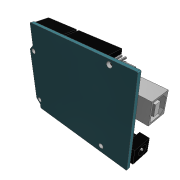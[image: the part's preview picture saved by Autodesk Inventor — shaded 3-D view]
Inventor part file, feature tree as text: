
AUTODESK INVENTOR PART (.ipt)
format: ipt  version: 2014 (Build 180170000, 170)  size: 910,848 bytes
history: native  units: mm
features: sketch x32, extrude x31, hole x1, chamfer x1, pattern_linear x1, plane x1, mirror x1, fillet x1
ambient origin geometry x8: Origin, YZ Plane, XZ Plane, XY Plane, X Axis, Y Axis, Z Axis, Center Point
bodies: Solid1 (feature_tree)
feature tree (69):
  extrude  "Extrusion1"  Depth=3.0mm
  extrude  "Extrusion2"  Depth=3.0mm
  extrude  "Extrusion3"  Depth=65.5mm
  extrude  "Extrusion4"  Depth=38.0mm
  extrude  "Extrusion5"  Depth=0.5mm
  extrude  "Extrusion6"  Depth=6.2mm
  extrude  "Extrusion7"  Depth=2.0mm TaperAngle=0.0deg
  hole  "Hole1"  [1 undecoded]
  extrude  "Extrusion8"  Depth=0.8mm
  extrude  "Extrusion9"  Depth=0.8mm
  extrude  "Extrusion10"  Depth=2.0mm
  extrude  "Extrusion11"  Depth=0.02mm TaperAngle=90.0deg
  extrude  "Extrusion12"  Depth=16.3mm
  extrude  "Extrusion13"  Depth=11.0mm TaperAngle=0.0deg
  extrude  "Extrusion14"  Depth=1.0mm
  extrude  "Extrusion15"  Depth=7.0mm
  extrude  "Extrusion16"  Depth=9.0mm TaperAngle=0.0deg
  extrude  "Extrusion17"  Depth=3.2mm
  extrude  "Extrusion18"  Depth=3.0mm
  extrude  "Extrusion19"  Depth=3.0mm
  chamfer  "Chamfer1"  Distance=11.0mm
  extrude  "Extrusion20"  Depth=8.0mm TaperAngle=0.0deg
  pattern_linear  "Rectangular Pattern1"  Spacing1=2.5mm  [1 undecoded]
  plane  "Work Plane1"
  mirror  "Mirror1"
  extrude  "Extrusion21"  Depth=13.5mm
  extrude  "Extrusion22"  Depth=0.75mm
  extrude  "Extrusion23"  Depth=1.0mm
  extrude  "Extrusion24"  Depth=2.65mm
  extrude  "Extrusion25"  Depth=1.0mm TaperAngle=0.0deg
  extrude  "Extrusion26"  Depth=0.75mm
  extrude  "Extrusion27"  Depth=1.0mm
  extrude  "Extrusion28"  Depth=2.61mm
  fillet  "Fillet1"  Radius=1.0mm
  extrude  "Extrusion29"  Depth=15.3mm
  extrude  "Extrusion30"  Depth=2.5mm
  extrude  "Extrusion31"  Depth=21.0mm
  sketch  "Sketch1"  dims[d1=53.5mm d3=3.0mm]
  sketch  "Sketch2"  dims[d5=6.0mm d6=3.0mm]
  sketch  "Sketch3"  dims[d7=12.5mm d9=65.5mm]
  sketch  "Sketch4"  dims[d10=65.5mm d11=38.0mm]
  sketch  "Sketch5"  dims[d12=32.0mm d13=0.5mm]
  sketch  "Sketch6"  dims[d14=2.0mm d15=0.0mm d16=6.2mm]
  sketch  "Sketch7"  dims[d17=6.2mm d18=2.0mm d19=0.0mm]
  sketch  "Sketch8"  dims[d20=3.14mm d21=1.5mm d22=0.0mm]
  sketch  "Sketch9"  dims[d23=2.0mm d24=0.8mm]
  sketch  "Sketch10"  dims[d25=2.0mm d26=0.8mm]
  sketch  "Sketch11"  dims[d27=0.8mm d28=2.0mm]
  sketch  "Sketch12"  dims[d29=0.02mm d30=90.0deg d31=0.02mm]
  sketch  "Sketch13"  dims[d32=0.4mm d33=0.0mm d34=16.3mm]
  sketch  "Sketch14"  dims[d35=12.0mm d36=11.0mm d37=0.0mm]
  sketch  "Sketch15"  dims[d39=1.0mm d40=1.0mm]
  sketch  "Sketch16"  dims[d41=10.0mm d43=7.0mm]
  sketch  "Sketch17"  dims[d44=6.0mm d45=9.0mm d46=0.0mm]
  sketch  "Sketch18"  dims[d47=6.0mm d48=3.2mm]
  sketch  "Sketch19"  dims[d49=9.0mm d50=0.0mm d51=3.0mm]
  sketch  "Sketch20"  dims[d52=3.0mm d53=3.0mm]
  sketch  "Sketch21"  dims[d54=3.0mm]
  sketch  "Sketch22"  dims[d55=3.0mm d56=6.0mm d57=4.0mm d58=2.0mm d59=90.0deg d60=8.0mm d61=20.594885mm]
  sketch  "Sketch23"  dims[d62=13.6mm]
  sketch  "Sketch24"  dims[d63=9.0mm d64=11.0mm d65=0.0mm]
  sketch  "Sketch25"  dims[d66=6.0mm d67=8.0mm d68=0.0mm]
  sketch  "Sketch26"  dims[d69=8.0mm d70=0.0mm]
  sketch  "Sketch27"  dims[d71=1.2mm]
  sketch  "Sketch28"  dims[d72=8.0mm d73=0.0mm]
  sketch  "Sketch29"  dims[d74=21.0mm]
  sketch  "Sketch30"  dims[d75=2.5mm]
  sketch  "Sketch31"  dims[d76=26.0mm]
  sketch  "Sketch32"  dims[d77=9.0mm d78=0.0mm d79=2.5mm d80=13.5mm d81=0.75mm d82=1.0mm d83=80.0mm d85=2.65mm d86=10.0mm d88=10.0mm d90=1.0mm d91=0.0mm d92=0.75mm d93=1.0mm d94=100.0mm d96=2.61mm d97=10.0mm d99=10.0mm d101=1.0mm d102=0.0mm d103=15.3mm d104=2.5mm d105=21.0mm d106=9.0mm d107=0.0mm d108=0.75mm d109=1.0mm d110=80.0mm d112=2.65mm d113=10.0mm d115=10.0mm d117=1.0mm d118=0.0mm d119=0.75mm d120=1.0mm d121=60.0mm d123=2.6mm d124=10.0mm d126=10.0mm d128=1.0mm d129=0.0mm d130=35.6mm d131=10.0mm d132=4.0mm d133=0.0mm d134=35.4mm d135=9.0mm d136=3.0mm d137=0.0mm d138=0.2mm d139=2.0mm d140=45.0deg d141=1.5mm d142=2.5mm d143=0.3mm d144=0.0mm d145=140.0mm d147=2.48mm d148=6.2mm d149=6.2mm d150=6.3mm d151=45.0mm d152=43.0mm d153=5.0mm d154=0.0mm d155=5.0mm d156=7.5mm d157=7.5mm d158=5.0mm d159=2.0mm d160=0.0mm d161=5.0mm d162=5.0mm d163=1.0mm d164=0.0mm d165=5.0mm d166=0.5mm d167=0.0mm d168=3.0mm d169=1.0mm d170=0.0mm d171=2.0mm d172=5.0mm d173=1.0mm d174=0.0mm d175=1.0mm d178=30.0mm d180=2.35mm d181=20.0mm d183=2.2mm d186=10.0mm d187=0.0mm d188=10.0mm d189=3.5mm d190=4.0mm d191=0.0mm d192=0.5mm d193=1.0mm d194=0.8mm d195=0.8mm d196=30.0mm d198=2.35mm d199=20.0mm d201=2.2mm d204=10.0mm d205=0.0mm d206=1.5mm d207=3.25mm d208=3.25mm d209=1.5mm d210=1.5mm d211=0.2mm d212=0.0mm d213=0.8mm d214=1.1mm d215=0.8mm d216=1.1mm d217=1.1mm d218=0.1mm d219=0.0mm]
note: 2 required parameter values undecoded (feature->parameter linkage not recoverable at this tier; creation-order binding heuristic only, values carry confidence <= 0.55)
